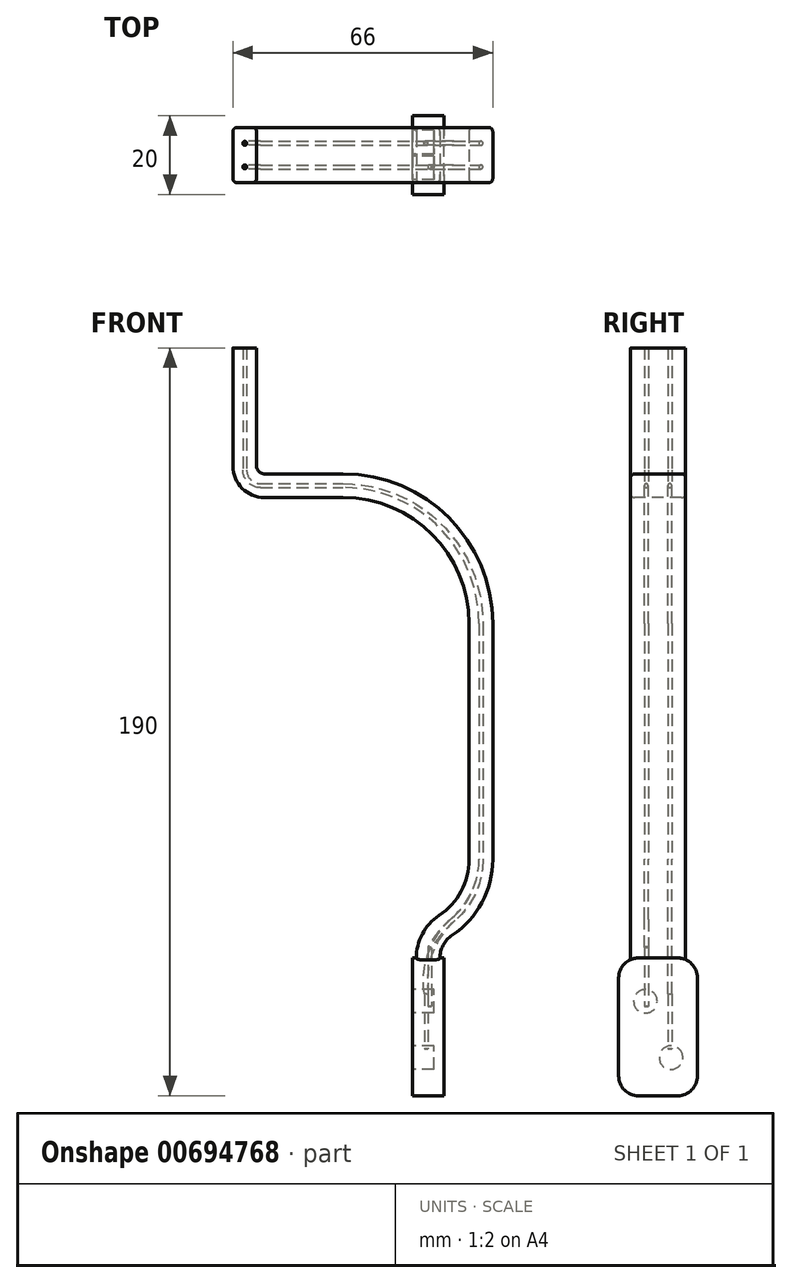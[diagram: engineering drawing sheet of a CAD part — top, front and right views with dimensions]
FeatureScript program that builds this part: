
annotation { "Feature Type Name" : "Feature", "Feature Type Description" : "" }
export const myFeature = defineFeature(function(context is Context, id is Id, definition is map)
    precondition{}
    {
        {
            var Q0;
            Q0=qCreatedBy(makeId("Front.planeOp"),FACE);
            var sketch = newSketch(context, id + "F0", { "sketchPlane" : qUnion([Q0])});
            skLineSegment(sketch, "E0", {"start": v(0, 50) * mm, "end": v(0, 20) * mm});
            skArc(sketch, "E1", {"start": v(0, 20) * mm, "mid": v(1.46, 16.46) * mm, "end": v(5, 15) * mm});
            skLineSegment(sketch, "E2", {"start": v(5, 15) * mm, "end": v(25, 15) * mm});
            skArc(sketch, "E3", {"start": v(25, 15) * mm, "mid": v(49.75, 4.75) * mm, "end": v(60, -20) * mm});
            skLineSegment(sketch, "E4", {"start": v(60, -20) * mm, "end": v(60, -80) * mm});
            skArc(sketch, "E5", {"start": v(60, -80) * mm, "mid": v(57.62, -89.46) * mm, "end": v(51.06, -96.67) * mm});
            skArc(sketch, "E6", {"start": v(51.06, -96.67) * mm, "mid": v(47.77, -100.27) * mm, "end": v(46.58, -105) * mm});
            skSolve(sketch);
        }
        {
            var Q0;
            Q0=qCreatedBy(makeId("Top.planeOp"),FACE);
            cPlane(context, id + "F1", {"entities" : qUnion([Q0]), "cplaneType" : CPlaneType.OFFSET, "offset" : 50 * mm, "width" : 150 * mm, "height" : 150 * mm});
        }
        {
            var Q0;
            Q0=qCreatedBy(id+"F1.planeOp",FACE);
            var sketch = newSketch(context, id + "F2", { "sketchPlane" : qUnion([Q0])});
            skLineSegment(sketch, "E7.bottom", {"start": v(-2, 7) * mm, "end": v(2, 7) * mm});
            skLineSegment(sketch, "E7.top", {"start": v(-2, -7) * mm, "end": v(2, -7) * mm});
            skLineSegment(sketch, "E7.left", {"start": v(-3, 6) * mm, "end": v(-3, -6) * mm});
            skLineSegment(sketch, "E7.right", {"start": v(3, 6) * mm, "end": v(3, -6) * mm});
            skPoint(sketch, "E8.visualSharp", {"position": v(-3, 7) * mm});
            skArc(sketch, "E8.filletArc", {"start": v(-2, 7) * mm, "mid": v(-2.7, 6.7) * mm, "end": v(-3, 6) * mm});
            skPoint(sketch, "E9.visualSharp", {"position": v(3, 7) * mm});
            skArc(sketch, "E9.filletArc", {"start": v(3, 6) * mm, "mid": v(2.7, 6.7) * mm, "end": v(2, 7) * mm});
            skPoint(sketch, "E10.visualSharp", {"position": v(3, -7) * mm});
            skArc(sketch, "E10.filletArc", {"start": v(2, -7) * mm, "mid": v(2.7, -6.7) * mm, "end": v(3, -6) * mm});
            skPoint(sketch, "E11.visualSharp", {"position": v(-3, -7) * mm});
            skArc(sketch, "E11.filletArc", {"start": v(-3, -6) * mm, "mid": v(-2.7, -6.7) * mm, "end": v(-2, -7) * mm});
            skSolve(sketch);
        }
        {
            var Q0;
            Q0=makeQuery(id+"F2.imprint","IMPRINT",FACE,{"disambiguationData":[TD([[makeQuery(id+"F2.imprint","IMPRINT",EDGE,{"derivedFrom":sQuery(id+"F2.wireOp",EDGE,"E7.bottom")}),-1.0]])]});
            var Q1;
            Q1=sQuery(id+"F0.wireOp",EDGE,"E0");
            var Q2;
            Q2=sQuery(id+"F0.wireOp",EDGE,"E1");
            var Q3;
            Q3=sQuery(id+"F0.wireOp",EDGE,"E2");
            var Q4;
            Q4=sQuery(id+"F0.wireOp",EDGE,"E3");
            var Q5;
            Q5=sQuery(id+"F0.wireOp",EDGE,"E4");
            var Q6;
            Q6=sQuery(id+"F0.wireOp",EDGE,"E5");
            var Q7;
            Q7=sQuery(id+"F0.wireOp",EDGE,"E6");
            sweep(context, id + "F3", {"profiles" : qUnion([Q0]), "path" : qUnion([Q1, Q2, Q3, Q4, Q5, Q6, Q7])});
        }
        {
            var Q0;
            Q0=makeQuery(id+"F3.opSweep","CAP_FACE",FACE,{"disambiguationData":[OSD([sQuery(id+"F0.wireOp",VERTEX,"E6.end"),sQuery(id+"F2.wireOp",EDGE,"E7.bottom"),sQuery(id+"F2.wireOp",EDGE,"E7.top"),sQuery(id+"F2.wireOp",EDGE,"E7.left"),sQuery(id+"F2.wireOp",EDGE,"E7.right"),sQuery(id+"F2.wireOp",EDGE,"E8.filletArc"),sQuery(id+"F2.wireOp",EDGE,"E9.filletArc"),sQuery(id+"F2.wireOp",EDGE,"E10.filletArc"),sQuery(id+"F2.wireOp",EDGE,"E11.filletArc")])],"isStart":false});
            var sketch = newSketch(context, id + "F4", { "sketchPlane" : qUnion([Q0])});
            skLineSegment(sketch, "E12.bottom", {"start": v(42.58, 10) * mm, "end": v(50.58, 10) * mm});
            skLineSegment(sketch, "E12.top", {"start": v(42.58, -10) * mm, "end": v(50.58, -10) * mm});
            skLineSegment(sketch, "E12.left", {"start": v(42.58, 10) * mm, "end": v(42.58, -10) * mm});
            skLineSegment(sketch, "E12.right", {"start": v(50.58, 10) * mm, "end": v(50.58, -10) * mm});
            skSolve(sketch);
        }
        {
            var Q0;
            Q0 = qSketchRegion(id + "F4", true);
            extrude(context, id + "F5", {"entities" : qUnion([Q0]), "operationType" : NewBodyOperationType.ADD, "depth" : 35 * mm, "offsetDistance" : 25 * mm});
        }
        {
            var Q0;
            Q0=makeQuery(id+"F5.opExtrude","CAP_EDGE",EDGE,{"disambiguationData":[OSD([sQuery(id+"F4.wireOp",EDGE,"E12.bottom")])],"isStart":false});
            fillet(context, id + "F6", {"entities" : qUnion([Q0]), "radius" : 5 * mm, "tangentPropagation" : true, "allowEdgeOverflow" : false});
        }
        {
            var Q0;
            Q0=makeQuery(id+"F5.opExtrude","CAP_EDGE",EDGE,{"disambiguationData":[OSD([sQuery(id+"F4.wireOp",EDGE,"E12.bottom")])],"isStart":true});
            fillet(context, id + "F7", {"entities" : qUnion([Q0]), "radius" : 5 * mm, "tangentPropagation" : true, "allowEdgeOverflow" : false});
        }
        {
            var Q0;
            Q0=makeQuery(id+"F5.opExtrude","CAP_EDGE",EDGE,{"disambiguationData":[OSD([sQuery(id+"F4.wireOp",EDGE,"E12.top")])],"isStart":false});
            fillet(context, id + "F8", {"entities" : qUnion([Q0]), "radius" : 5 * mm, "tangentPropagation" : true, "allowEdgeOverflow" : false});
        }
        {
            var Q0;
            Q0=makeQuery(id+"F5.opExtrude","CAP_EDGE",EDGE,{"disambiguationData":[OSD([sQuery(id+"F4.wireOp",EDGE,"E12.top")])],"isStart":true});
            fillet(context, id + "F9", {"entities" : qUnion([Q0]), "radius" : 5 * mm, "tangentPropagation" : true, "allowEdgeOverflow" : false});
        }
        {
            var Q0;
            Q0=qCreatedBy(makeId("Front.planeOp"),FACE);
            cPlane(context, id + "F10", {"entities" : qUnion([Q0]), "cplaneType" : CPlaneType.OFFSET, "offset" : 3 * mm, "width" : 150 * mm, "height" : 150 * mm});
        }
        {
            var Q0;
            Q0=makeQuery(id+"F3.opSweep","CAP_FACE",FACE,{"disambiguationData":[OSD([sQuery(id+"F0.wireOp",VERTEX,"E0.start"),sQuery(id+"F2.wireOp",EDGE,"E7.bottom"),sQuery(id+"F2.wireOp",EDGE,"E7.top"),sQuery(id+"F2.wireOp",EDGE,"E7.left"),sQuery(id+"F2.wireOp",EDGE,"E7.right"),sQuery(id+"F2.wireOp",EDGE,"E8.filletArc"),sQuery(id+"F2.wireOp",EDGE,"E9.filletArc"),sQuery(id+"F2.wireOp",EDGE,"E10.filletArc"),sQuery(id+"F2.wireOp",EDGE,"E11.filletArc")])],"isStart":true});
            var sketch = newSketch(context, id + "F11", { "sketchPlane" : qUnion([Q0])});
            skPoint(sketch, "E13", {"position": v(0, -3) * mm});
            skPoint(sketch, "E14", {"position": v(0, 3) * mm});
            skSolve(sketch);
        }
        {
            var Q0;
            Q0=qCreatedBy(id+"F10.planeOp",FACE);
            var sketch = newSketch(context, id + "F12", { "sketchPlane" : qUnion([Q0])});
            skLineSegment(sketch, "E15", {"start": v(0, 50) * mm, "end": v(0, 19) * mm});
            skArc(sketch, "E16", {"start": v(0, 19) * mm, "mid": v(1.17, 16.17) * mm, "end": v(4, 15) * mm});
            skLineSegment(sketch, "E17", {"start": v(4, 15) * mm, "end": v(25, 15) * mm});
            skArc(sketch, "E18", {"start": v(25, 15) * mm, "mid": v(49.75, 4.75) * mm, "end": v(60, -20) * mm});
            skLineSegment(sketch, "E19", {"start": v(60, -20) * mm, "end": v(60, -80) * mm});
            skArc(sketch, "E20", {"start": v(60, -80) * mm, "mid": v(58.17, -88.37) * mm, "end": v(53, -95.2) * mm});
            skArc(sketch, "E21", {"start": v(53, -95.2) * mm, "mid": v(49.72, -98.5) * mm, "end": v(47, -102.26) * mm});
            skLineSegment(sketch, "E22", {"start": v(47, -102.26) * mm, "end": v(47, -117.26) * mm});
            skSolve(sketch);
        }
        {
            var Q0;
            {var subQ0=sQuery(id+"F0.wireOp",VERTEX,"E0.start");Q0=makeQuery(id+"F11.imprint","IMPRINT",FACE,{"disambiguationData":[TD([[makeQuery(id+"F11.imprint","IMPRINT",EDGE,{"derivedFrom":makeQuery(id+"F3.opSweep","CAP_EDGE",EDGE,{"disambiguationData":[OSD([subQ0,sQuery(id+"F2.wireOp",EDGE,"E7.bottom")])],"isStart":true})}),-1.0]])]});}
            var sketch = newSketch(context, id + "F13", { "sketchPlane" : qUnion([Q0])});
            skCircle(sketch, "E23", {"center": v(0, -3) * mm, "radius": 0.5 * mm});
            skSolve(sketch);
        }
        {
            var Q0;
            Q0 = qSketchRegion(id + "F13", true);
            var Q1;
            Q1 = qConstructionFilter(qBodyType(qCreatedBy(id + "F12" ,EDGE), BodyType.WIRE), ConstructionObject.NO);
            sweep(context, id + "F14", {"profiles" : qUnion([Q0]), "path" : qUnion([Q1])});
        }
        {
            var Q0;
            Q0=qCreatedBy(makeId("Front.planeOp"),FACE);
            cPlane(context, id + "F15", {"entities" : qUnion([Q0]), "cplaneType" : CPlaneType.OFFSET, "offset" : 3 * mm, "oppositeDirection" : true, "width" : 150 * mm, "height" : 150 * mm});
        }
        {
            var Q0;
            Q0=qCreatedBy(id+"F15.planeOp",FACE);
            var sketch = newSketch(context, id + "F16", { "sketchPlane" : qUnion([Q0])});
            skLineSegment(sketch, "E24", {"start": v(0, 50) * mm, "end": v(0, 19) * mm});
            skArc(sketch, "E25", {"start": v(0, 19) * mm, "mid": v(1.17, 16.17) * mm, "end": v(4, 15) * mm});
            skLineSegment(sketch, "E26", {"start": v(4, 15) * mm, "end": v(25, 15) * mm});
            skArc(sketch, "E27", {"start": v(25, 15) * mm, "mid": v(49.75, 4.75) * mm, "end": v(60, -20) * mm});
            skLineSegment(sketch, "E28", {"start": v(60, -20) * mm, "end": v(60, -80) * mm});
            skArc(sketch, "E29", {"start": v(60, -80) * mm, "mid": v(58.2, -88.3) * mm, "end": v(53.1, -95.1) * mm});
            skArc(sketch, "E30", {"start": v(53.1, -95.1) * mm, "mid": v(47.17, -103.7) * mm, "end": v(46.1, -114.1) * mm});
            skLineSegment(sketch, "E31", {"start": v(46.1, -114.1) * mm, "end": v(46.1, -128.1) * mm});
            skSolve(sketch);
        }
        {
            var Q0;
            {var subQ0=sQuery(id+"F0.wireOp",VERTEX,"E0.start");Q0=makeQuery(id+"F11.imprint","IMPRINT",FACE,{"disambiguationData":[TD([[makeQuery(id+"F11.imprint","IMPRINT",EDGE,{"derivedFrom":makeQuery(id+"F3.opSweep","CAP_EDGE",EDGE,{"disambiguationData":[OSD([subQ0,sQuery(id+"F2.wireOp",EDGE,"E7.bottom")])],"isStart":true})}),-1.0]])]});}
            var sketch = newSketch(context, id + "F17", { "sketchPlane" : qUnion([Q0])});
            skCircle(sketch, "E32", {"center": v(0, 3) * mm, "radius": 0.5 * mm});
            skSolve(sketch);
        }
        {
            var Q0;
            Q0=makeQuery(id+"F17.imprint","IMPRINT",FACE,{"disambiguationData":[TD([[makeQuery(id+"F17.imprint","IMPRINT",EDGE,{"derivedFrom":sQuery(id+"F17.wireOp",EDGE,"E32")}),1.0]])]});
            var Q1;
            Q1=sQuery(id+"F16.wireOp",EDGE,"E24");
            var Q2;
            Q2=sQuery(id+"F16.wireOp",EDGE,"E25");
            var Q3;
            Q3=sQuery(id+"F16.wireOp",EDGE,"E26");
            var Q4;
            Q4=sQuery(id+"F16.wireOp",EDGE,"E27");
            var Q5;
            Q5=sQuery(id+"F16.wireOp",EDGE,"E28");
            var Q6;
            Q6=sQuery(id+"F16.wireOp",EDGE,"E29");
            var Q7;
            Q7=sQuery(id+"F16.wireOp",EDGE,"E30");
            var Q8;
            Q8=sQuery(id+"F16.wireOp",EDGE,"E31");
            sweep(context, id + "F18", {"profiles" : qUnion([Q0]), "path" : qUnion([Q1, Q2, Q3, Q4, Q5, Q6, Q7, Q8])});
        }
        {
            var Q0;
            Q0=makeQuery(id+"F5.opExtrude","SWEPT_FACE",FACE,{"disambiguationData":[OSD([sQuery(id+"F4.wireOp",EDGE,"E12.right")])]});
            cPlane(context, id + "F19", {"entities" : qUnion([Q0]), "cplaneType" : CPlaneType.OFFSET, "offset" : 4.5 * mm, "oppositeDirection" : true, "width" : 150 * mm, "height" : 150 * mm});
        }
        {
            var Q0;
            Q0=qCreatedBy(id+"F19.planeOp",FACE);
            var sketch = newSketch(context, id + "F20", { "sketchPlane" : qUnion([Q0])});
            skCircle(sketch, "E33", {"center": v(3.3, -130.3) * mm, "radius": 3 * mm});
            skCircle(sketch, "E34", {"center": v(-3.2, -116) * mm, "radius": 3 * mm});
            skSolve(sketch);
        }
        {
            var Q0;
            Q0 = qSketchRegion(id + "F20", true);
            extrude(context, id + "F21", {"entities" : qUnion([Q0]), "depth" : 2 * mm, "offsetDistance" : 25 * mm, "hasSecondDirection" : true, "secondDirectionOppositeDirection" : true, "secondDirectionDepth" : 3.5 * mm});
        }
    });
